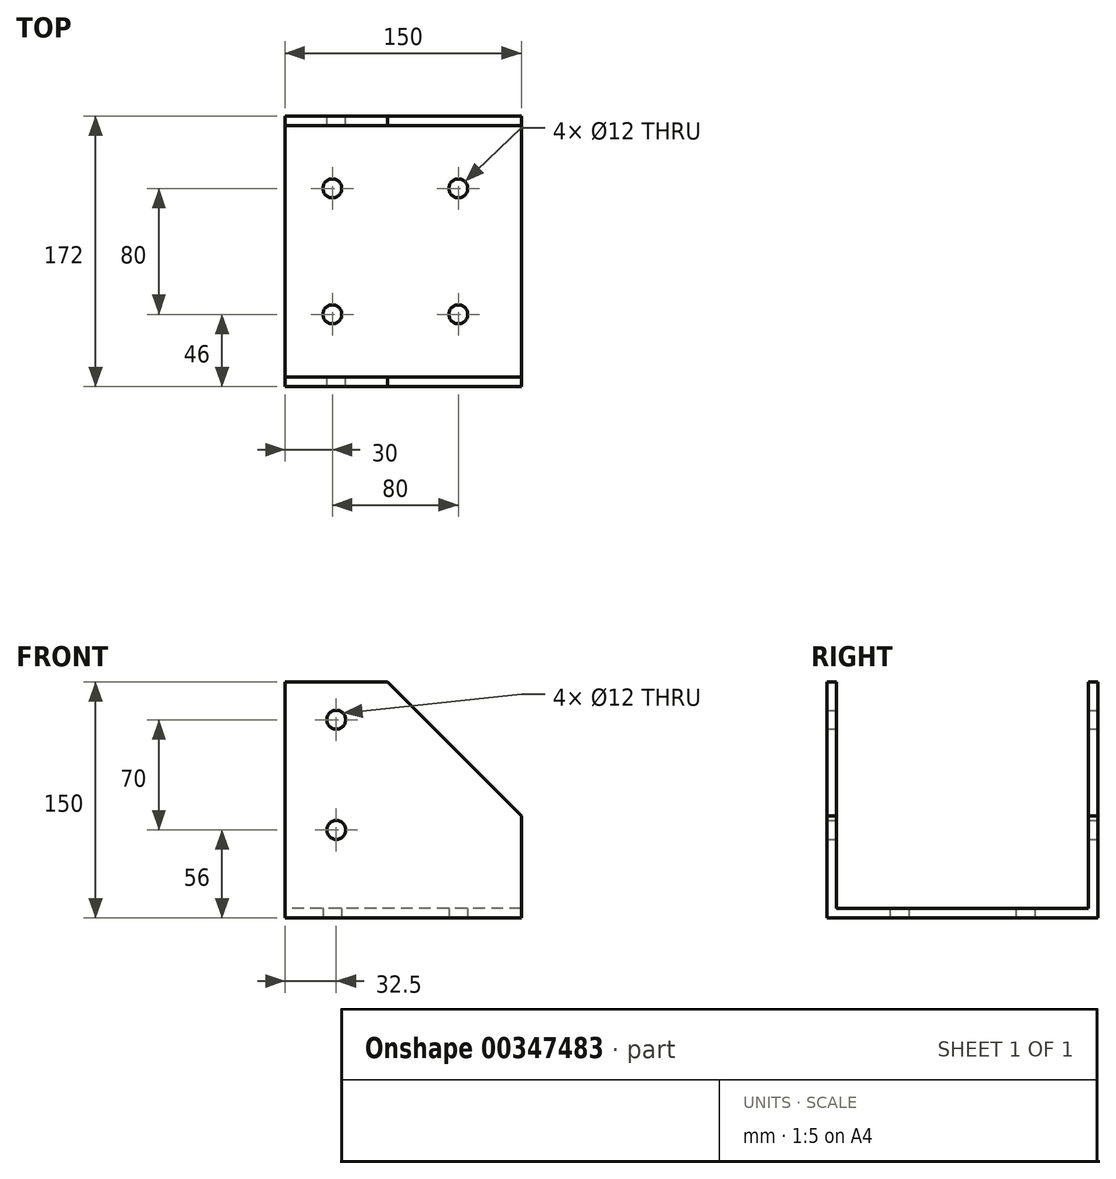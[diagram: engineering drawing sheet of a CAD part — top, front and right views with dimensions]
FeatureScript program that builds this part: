
annotation { "Feature Type Name" : "Feature", "Feature Type Description" : "" }
export const myFeature = defineFeature(function(context is Context, id is Id, definition is map)
    precondition{}
    {
        {
            var Q0;
            Q0=qCreatedBy(makeId("Front.planeOp"),FACE);
            var sketch = newSketch(context, id + "F0", { "sketchPlane" : qUnion([Q0])});
            skLineSegment(sketch, "E0.left", {"start": v(0, 0) * mm, "end": v(0, 0) * mm});
            skLineSegment(sketch, "E1.bottom", {"start": v(0, 0) * mm, "end": v(65, 0) * mm, "construction": true});
            skLineSegment(sketch, "E1.left", {"start": v(0, 0) * mm, "end": v(0, 150) * mm, "construction": true});
            skLineSegment(sketch, "E1.right", {"start": v(65, 0) * mm, "end": v(65, 150) * mm, "construction": true});
            skLineSegment(sketch, "E2", {"start": v(32.5, 150) * mm, "end": v(32.5, 0) * mm, "construction": true});
            skLineSegment(sketch, "E3.0", {"start": v(0, 56) * mm, "end": v(65, 56) * mm, "construction": true});
            skLineSegment(sketch, "E4.0", {"start": v(0, 126) * mm, "end": v(65, 126) * mm, "construction": true});
            skCircle(sketch, "E5", {"center": v(32.5, 126) * mm, "radius": 6 * mm});
            skCircle(sketch, "E6", {"center": v(32.5, 56) * mm, "radius": 6 * mm});
            skLineSegment(sketch, "E7", {"start": v(0, 0) * mm, "end": v(150, 0) * mm});
            skLineSegment(sketch, "E8", {"start": v(150, 0) * mm, "end": v(150, 65) * mm});
            skLineSegment(sketch, "E9", {"start": v(0, 0) * mm, "end": v(0, 150) * mm});
            skLineSegment(sketch, "E10", {"start": v(0, 150) * mm, "end": v(65, 150) * mm});
            skLineSegment(sketch, "E11", {"start": v(65, 150) * mm, "end": v(150, 65) * mm});
            skSolve(sketch);
        }
        {
            var Q0;
            Q0=makeQuery(id+"F0.imprint","IMPRINT",FACE,{"disambiguationData":[TD([[makeQuery(id+"F0.imprint","IMPRINT",EDGE,{"derivedFrom":sQuery(id+"F0.wireOp",EDGE,"E5")}),-1.0]])]});
            extrude(context, id + "F1", {"entities" : qUnion([Q0]), "endBound" : BoundingType.SYMMETRIC, "depth" : (160 + 6 + 6) * mm});
        }
        {
            var Q0;
            Q0=makeQuery(id+"F1.opExtrude","SWEPT_FACE",FACE,{"disambiguationData":[OSD([sQuery(id+"F0.wireOp",EDGE,"E9")])]});
            var sketch = newSketch(context, id + "F2", { "sketchPlane" : qUnion([Q0])});
            skLineSegment(sketch, "E12.0", {"start": v(80, 150) * mm, "end": v(-80, 150) * mm});
            skLineSegment(sketch, "E13.0", {"start": v(-80, 6) * mm, "end": v(-80, 150) * mm});
            skLineSegment(sketch, "E13.1", {"start": v(80, 6) * mm, "end": v(-80, 6) * mm});
            skLineSegment(sketch, "E13.2", {"start": v(80, 6) * mm, "end": v(80, 150) * mm});
            skLineSegment(sketch, "E14", {"start": v(0, 0) * mm, "end": v(0, 155.8) * mm, "construction": true});
            skPoint(sketch, "E14.endSnap0", {"position": v(0, 150) * mm});
            skSolve(sketch);
        }
        {
            var Q0;
            Q0=makeQuery(id+"F2.imprint","IMPRINT",FACE,{"disambiguationData":[TD([[makeQuery(id+"F2.imprint","IMPRINT",EDGE,{"derivedFrom":sQuery(id+"F2.wireOp",EDGE,"E12.0")}),1.0]])]});
            extrude(context, id + "F3", {"entities" : qUnion([Q0]), "operationType" : NewBodyOperationType.REMOVE, "endBound" : BoundingType.THROUGH_ALL, "oppositeDirection" : true, "depth" : 25 * mm});
        }
        {
            var Q0;
            Q0=makeQuery(id+"F1.opExtrude","SWEPT_FACE",FACE,{"disambiguationData":[OSD([sQuery(id+"F0.wireOp",EDGE,"E7")])]});
            var sketch = newSketch(context, id + "F4", { "sketchPlane" : qUnion([Q0])});
            skLineSegment(sketch, "E15", {"start": v(150, 0) * mm, "end": v(0, 0) * mm, "construction": true});
            skLineSegment(sketch, "E16", {"start": v(110, 56.15) * mm, "end": v(110, -52.77) * mm, "construction": true});
            skLineSegment(sketch, "E17", {"start": v(30, 48.2) * mm, "end": v(30, -50.36) * mm, "construction": true});
            skLineSegment(sketch, "E18", {"start": v(141.15, 40) * mm, "end": v(17.53, 40) * mm, "construction": true});
            skLineSegment(sketch, "E19", {"start": v(132.71, -40) * mm, "end": v(18.5, -40) * mm, "construction": true});
            skCircle(sketch, "E20", {"center": v(110, 40) * mm, "radius": 6 * mm});
            skCircle(sketch, "E21", {"center": v(110, -40) * mm, "radius": 6 * mm});
            skCircle(sketch, "E22", {"center": v(30, 40) * mm, "radius": 6 * mm});
            skCircle(sketch, "E23", {"center": v(30, -40) * mm, "radius": 6 * mm});
            skSolve(sketch);
        }
        {
            var Q0;
            Q0=makeQuery(id+"F4.imprint","IMPRINT",FACE,{"disambiguationData":[TD([[makeQuery(id+"F4.imprint","IMPRINT",EDGE,{"derivedFrom":sQuery(id+"F4.wireOp",EDGE,"E20")}),1.0]])]});
            var Q1;
            Q1=makeQuery(id+"F4.imprint","IMPRINT",FACE,{"disambiguationData":[TD([[makeQuery(id+"F4.imprint","IMPRINT",EDGE,{"derivedFrom":sQuery(id+"F4.wireOp",EDGE,"E21")}),1.0]])]});
            var Q2;
            Q2=makeQuery(id+"F4.imprint","IMPRINT",FACE,{"disambiguationData":[TD([[makeQuery(id+"F4.imprint","IMPRINT",EDGE,{"derivedFrom":sQuery(id+"F4.wireOp",EDGE,"E22")}),1.0]])]});
            var Q3;
            Q3=makeQuery(id+"F4.imprint","IMPRINT",FACE,{"disambiguationData":[TD([[makeQuery(id+"F4.imprint","IMPRINT",EDGE,{"derivedFrom":sQuery(id+"F4.wireOp",EDGE,"E23")}),1.0]])]});
            extrude(context, id + "F5", {"entities" : qUnion([Q0, Q1, Q2, Q3]), "operationType" : NewBodyOperationType.REMOVE, "endBound" : BoundingType.THROUGH_ALL, "oppositeDirection" : true, "depth" : 25 * mm});
        }
    });
